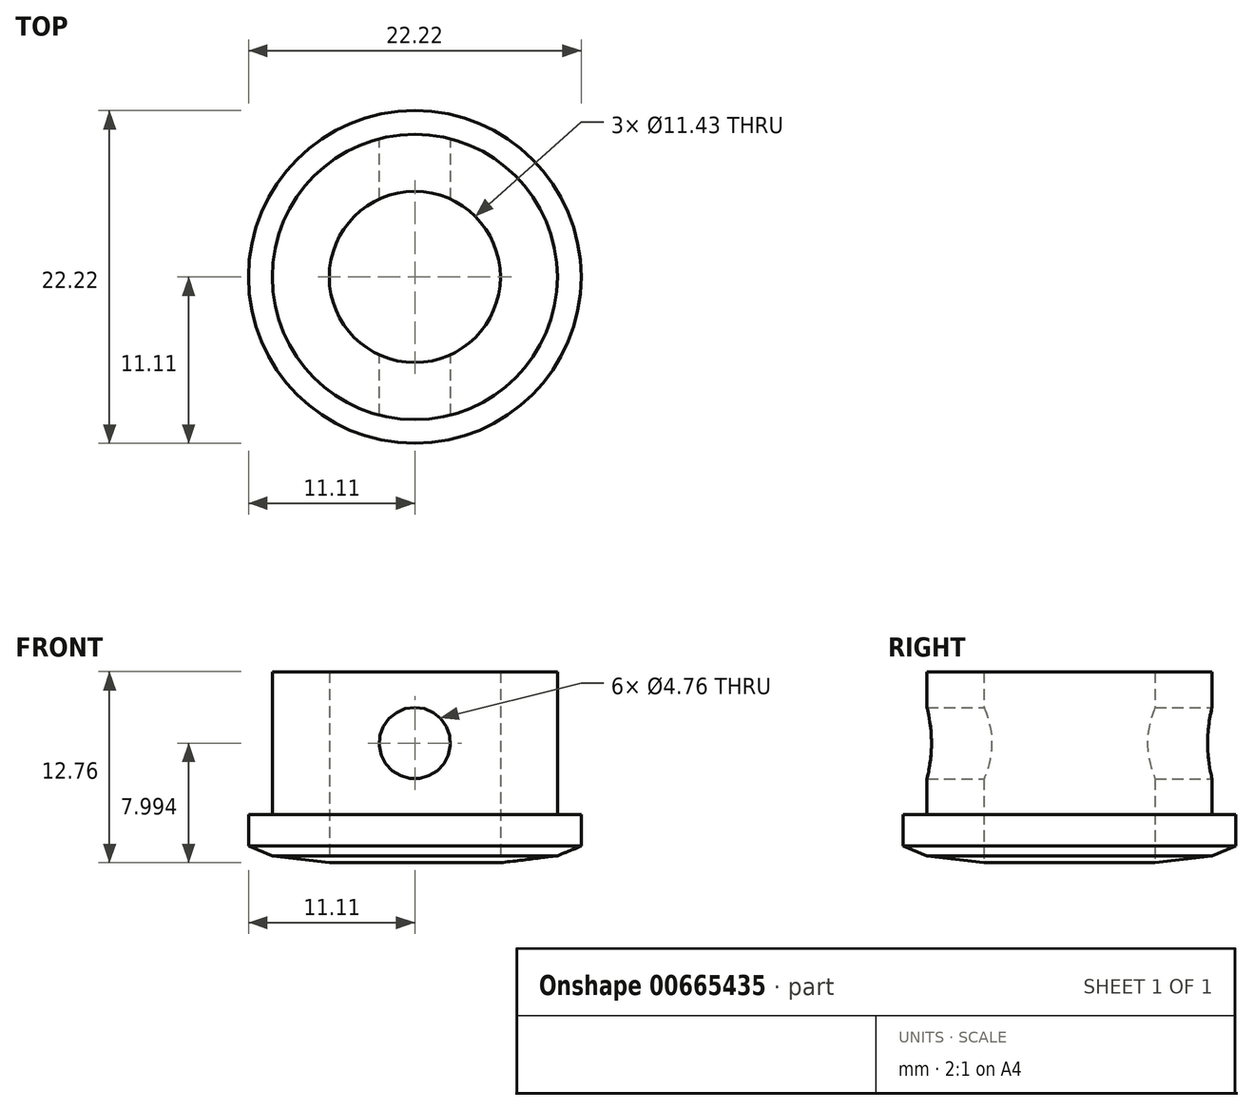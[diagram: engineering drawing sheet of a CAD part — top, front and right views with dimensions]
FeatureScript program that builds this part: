
annotation { "Feature Type Name" : "Feature", "Feature Type Description" : "" }
export const myFeature = defineFeature(function(context is Context, id is Id, definition is map)
    precondition{}
    {
        {
            var Q0;
            Q0=qCreatedBy(makeId("Front.planeOp"),FACE);
            var sketch = newSketch(context, id + "F0", { "sketchPlane" : qUnion([Q0])});
            skLineSegment(sketch, "E0", {"start": v(0, 11.65) * mm, "end": v(-9.52, 11.65) * mm});
            skLineSegment(sketch, "E1", {"start": v(-9.53, 11.65) * mm, "end": v(-9.53, 2.12) * mm});
            skLineSegment(sketch, "E2", {"start": v(-9.53, 2.12) * mm, "end": v(-11.11, 2.12) * mm});
            skLineSegment(sketch, "E3", {"start": v(-11.11, 2.12) * mm, "end": v(-11.11, 0) * mm});
            skLineSegment(sketch, "E4", {"start": v(-11.11, 0) * mm, "end": v(-9.53, -0.64) * mm});
            skLineSegment(sketch, "E5", {"start": v(-9.53, -0.64) * mm, "end": v(-4.76, -1.23) * mm});
            skLineSegment(sketch, "E6", {"start": v(-4.76, -1.23) * mm, "end": v(0, -1.23) * mm});
            skLineSegment(sketch, "E7", {"start": v(0, 11.65) * mm, "end": v(0, -1.23) * mm});
            skSolve(sketch);
        }
        {
            var Q0;
            Q0 = qSketchRegion(id + "F0", true);
            var Q1;
            Q1=sQuery(id+"F0.wireOp",EDGE,"E7");
            revolve(context, id + "F1", {"entities" : qUnion([Q0]), "axis" : qUnion([Q1]), "revolveType" : RevolveType.FULL});
        }
        {
            var Q0;
            Q0=qCreatedBy(makeId("Front.planeOp"),FACE);
            var sketch = newSketch(context, id + "F2", { "sketchPlane" : qUnion([Q0])});
            skCircle(sketch, "E8", {"center": v(0, 6.88) * mm, "radius": 2.38 * mm});
            skSolve(sketch);
        }
        {
            var Q0;
            Q0 = qSketchRegion(id + "F2", true);
            extrude(context, id + "F3", {"entities" : qUnion([Q0]), "operationType" : NewBodyOperationType.REMOVE, "depth" : 25.4 * mm, "offsetDistance" : 25.4 * mm, "symmetric" : true});
        }
        {
            var Q0;
            Q0=qCreatedBy(makeId("Top.planeOp"),FACE);
            var sketch = newSketch(context, id + "F4", { "sketchPlane" : qUnion([Q0])});
            skCircle(sketch, "E9", {"center": v(0, 0) * mm, "radius": 5.72 * mm});
            skSolve(sketch);
        }
        {
            var Q0;
            Q0 = qSketchRegion(id + "F4", true);
            extrude(context, id + "F5", {"entities" : qUnion([Q0]), "operationType" : NewBodyOperationType.REMOVE, "depth" : 25.4 * mm, "offsetDistance" : 25.4 * mm, "symmetric" : true});
        }
    });
